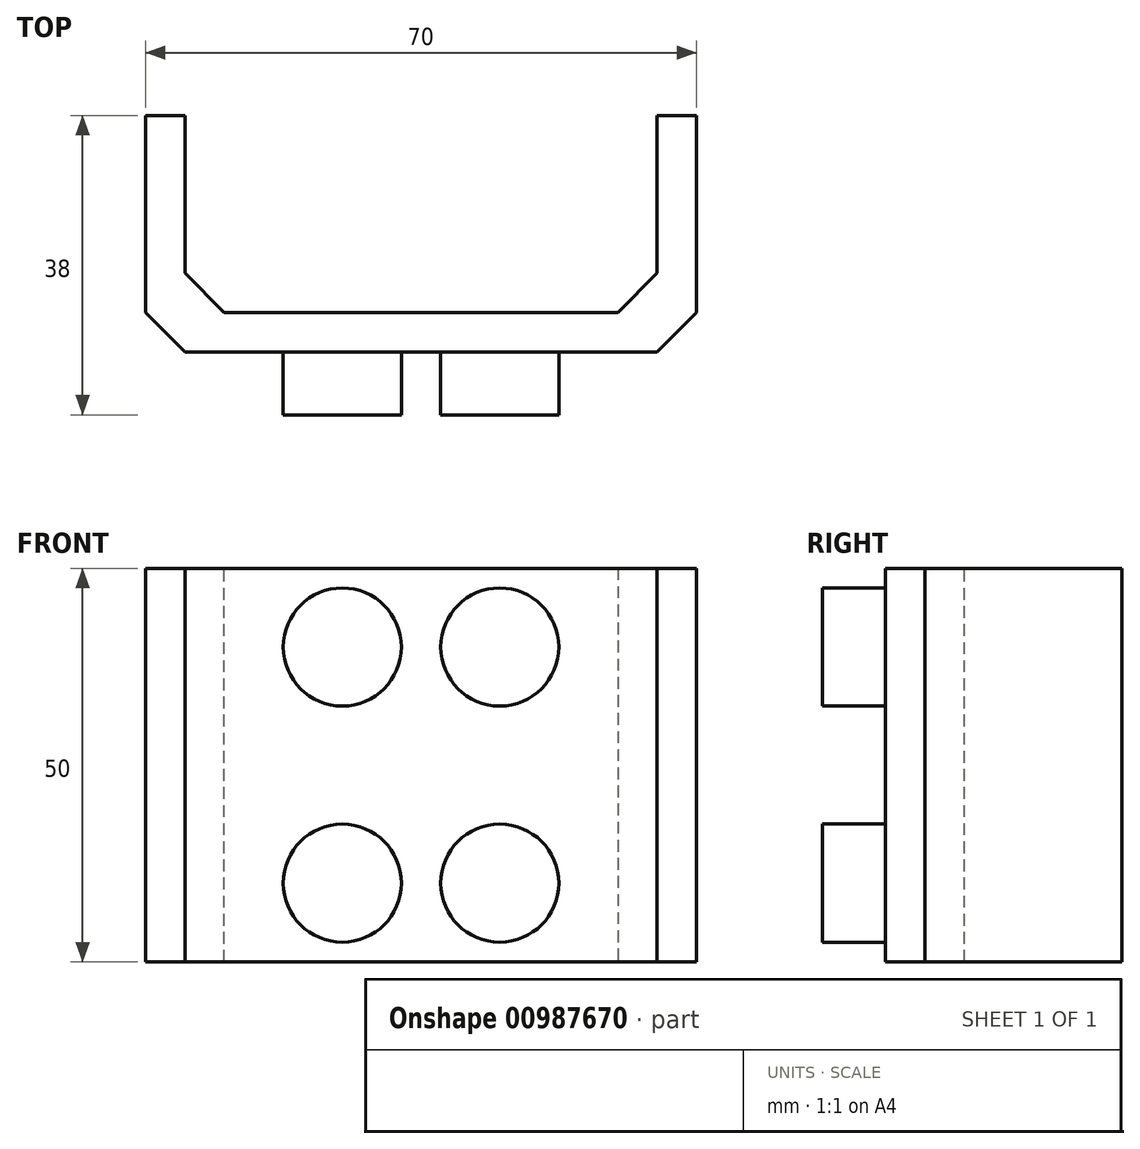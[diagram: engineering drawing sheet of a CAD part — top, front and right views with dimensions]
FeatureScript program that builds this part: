
annotation { "Feature Type Name" : "Feature", "Feature Type Description" : "" }
export const myFeature = defineFeature(function(context is Context, id is Id, definition is map)
    precondition{}
    {
        {
            var Q0;
            Q0=qCreatedBy(makeId("Top.planeOp"),FACE);
            var sketch = newSketch(context, id + "F0", { "sketchPlane" : qUnion([Q0])});
            skLineSegment(sketch, "E0", {"start": v(-35, 19) * mm, "end": v(-35, -11) * mm});
            skLineSegment(sketch, "E1", {"start": v(-35, -11) * mm, "end": v(0, -11) * mm});
            skLineSegment(sketch, "E2", {"start": v(0, -6) * mm, "end": v(-30, -6) * mm});
            skLineSegment(sketch, "E3", {"start": v(-30, -6) * mm, "end": v(-30, 19) * mm});
            skLineSegment(sketch, "E4", {"start": v(-30, 19) * mm, "end": v(-35, 19) * mm});
            skLineSegment(sketch, "E5.MirrorCS", {"start": v(30, -6) * mm, "end": v(30, 19) * mm});
            skLineSegment(sketch, "E6.MirrorCS", {"start": v(30, 19) * mm, "end": v(35, 19) * mm});
            skLineSegment(sketch, "E7.MirrorCS", {"start": v(35, 19) * mm, "end": v(35, -11) * mm});
            skLineSegment(sketch, "E8.MirrorCS", {"start": v(35, -11) * mm, "end": v(0, -11) * mm});
            skLineSegment(sketch, "E9.MirrorCS", {"start": v(0, -6) * mm, "end": v(30, -6) * mm});
            skSolve(sketch);
        }
        {
            var Q0;
            Q0 = qSketchRegion(id + "F0", true);
            extrude(context, id + "F1", {"entities" : qUnion([Q0]), "depth" : 50 * mm, "offsetDistance" : 25 * mm});
        }
        {
            var Q0;
            Q0=makeQuery(id+"F1.opExtrude","SWEPT_EDGE",EDGE,{"disambiguationData":[OSD([sQuery(id+"F0.wireOp",EDGE,"E2"),sQuery(id+"F0.wireOp",EDGE,"E3")])]});
            var Q1;
            Q1=makeQuery(id+"F1.opExtrude","SWEPT_EDGE",EDGE,{"disambiguationData":[OSD([sQuery(id+"F0.wireOp",EDGE,"E5.MirrorCS"),sQuery(id+"F0.wireOp",EDGE,"E9.MirrorCS")])]});
            var Q2;
            Q2=makeQuery(id+"F1.opExtrude","SWEPT_EDGE",EDGE,{"disambiguationData":[OSD([sQuery(id+"F0.wireOp",EDGE,"E0"),sQuery(id+"F0.wireOp",EDGE,"E1")])]});
            var Q3;
            Q3=makeQuery(id+"F1.opExtrude","SWEPT_EDGE",EDGE,{"disambiguationData":[OSD([sQuery(id+"F0.wireOp",EDGE,"E7.MirrorCS"),sQuery(id+"F0.wireOp",EDGE,"E8.MirrorCS")])]});
            chamfer(context, id + "F2", {"entities" : qUnion([Q0, Q1, Q2, Q3]), "width" : 5 * mm, "tangentPropagation" : true});
        }
        {
            var Q0;
            Q0=makeQuery(id+"F1.opExtrude","SWEPT_FACE",FACE,{"disambiguationData":[OSD([sQuery(id+"F0.wireOp",EDGE,"E1"),sQuery(id+"F0.wireOp",EDGE,"E8.MirrorCS")])]});
            var sketch = newSketch(context, id + "F3", { "sketchPlane" : qUnion([Q0])});
            skCircle(sketch, "E10", {"center": v(-10, 40) * mm, "radius": 7.5 * mm});
            skCircle(sketch, "E11", {"center": v(-10, 10) * mm, "radius": 7.5 * mm});
            skCircle(sketch, "E12.MirrorC", {"center": v(10, 40) * mm, "radius": 7.5 * mm});
            skCircle(sketch, "E13.MirrorC", {"center": v(10, 10) * mm, "radius": 7.5 * mm});
            skSolve(sketch);
        }
        {
            var Q0;
            Q0 = qSketchRegion(id + "F3", true);
            extrude(context, id + "F4", {"entities" : qUnion([Q0]), "operationType" : NewBodyOperationType.ADD, "depth" : (13 - 5) * mm, "offsetDistance" : 25 * mm});
        }
    });
